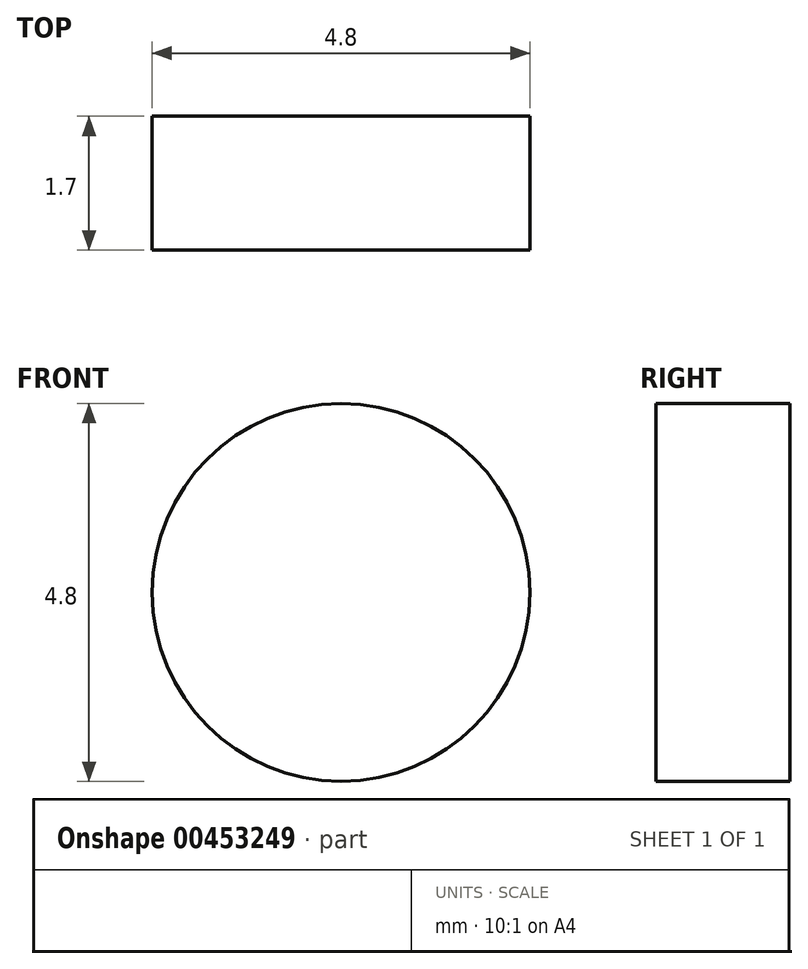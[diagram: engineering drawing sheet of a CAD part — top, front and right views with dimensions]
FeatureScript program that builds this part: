
annotation { "Feature Type Name" : "Feature", "Feature Type Description" : "" }
export const myFeature = defineFeature(function(context is Context, id is Id, definition is map)
    precondition{}
    {
        {
            var Q0;
            Q0=qCreatedBy(makeId("Front.planeOp"),FACE);
            var sketch = newSketch(context, id + "F0", { "sketchPlane" : qUnion([Q0])});
            skCircle(sketch, "E0", {"center": v(0, 0) * mm, "radius": 2.4 * mm});
            skSolve(sketch);
        }
        {
            var Q0;
            Q0 = qSketchRegion(id + "F0", true);
            extrude(context, id + "F1", {"entities" : qUnion([Q0]), "depth" : 1.7 * mm});
        }
    });
